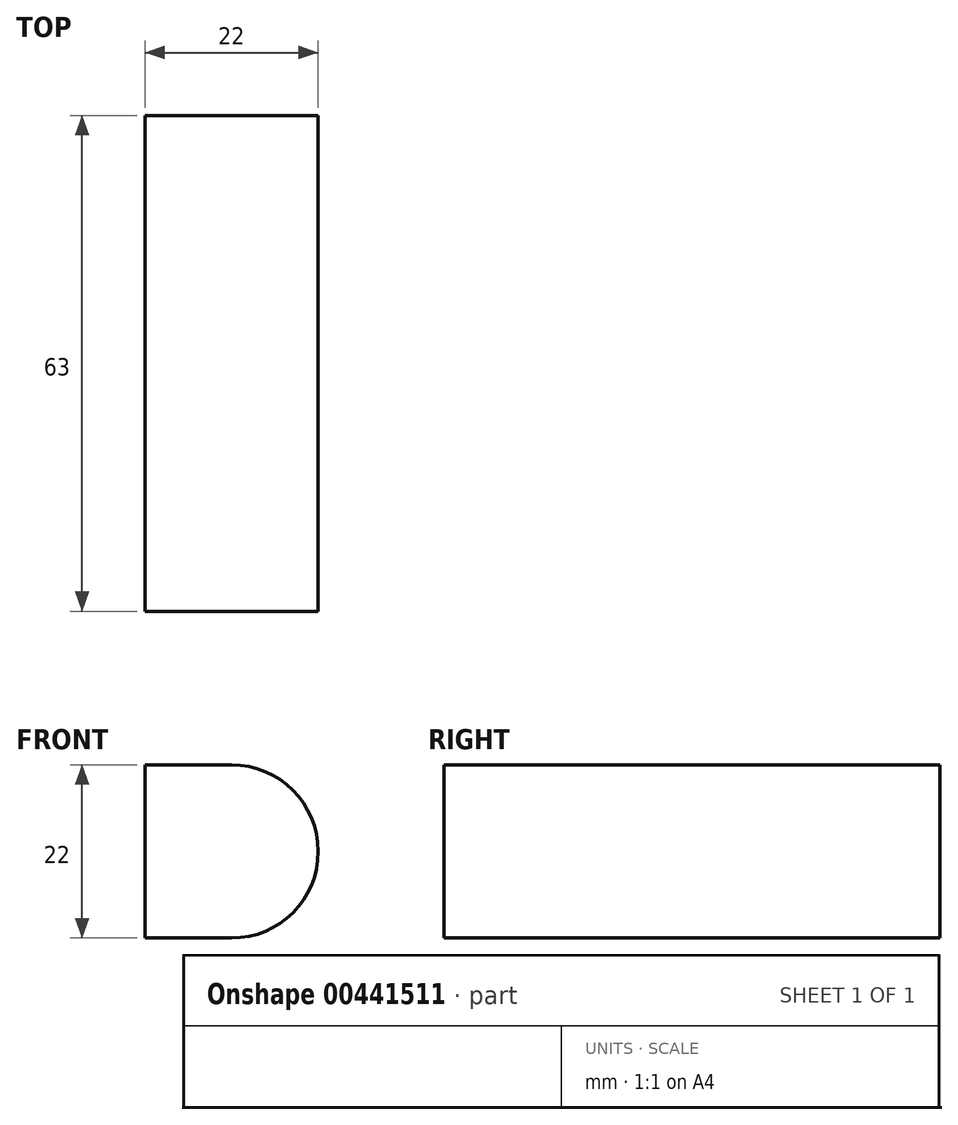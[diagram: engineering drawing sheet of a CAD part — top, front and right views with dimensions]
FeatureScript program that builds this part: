
annotation { "Feature Type Name" : "Feature", "Feature Type Description" : "" }
export const myFeature = defineFeature(function(context is Context, id is Id, definition is map)
    precondition{}
    {
        {
            var Q0;
            Q0=qCreatedBy(makeId("Front.planeOp"),FACE);
            var sketch = newSketch(context, id + "F0", { "sketchPlane" : qUnion([Q0])});
            skArc(sketch, "E0", {"start": v(0, -11) * mm, "mid": v(11, 0) * mm, "end": v(0, 11) * mm});
            skLineSegment(sketch, "E1", {"start": v(0, -11) * mm, "end": v(-11, -11) * mm});
            skLineSegment(sketch, "E2", {"start": v(-11, -11) * mm, "end": v(-11, 11) * mm});
            skLineSegment(sketch, "E3", {"start": v(-11, 11) * mm, "end": v(0, 11) * mm});
            skSolve(sketch);
        }
        {
            var Q0;
            Q0=qSketchRegion(id+"F0",true);
            extrude(context, id + "F1", {"entities" : qUnion([Q0]), "depth" : 63 * mm});
        }
    });
